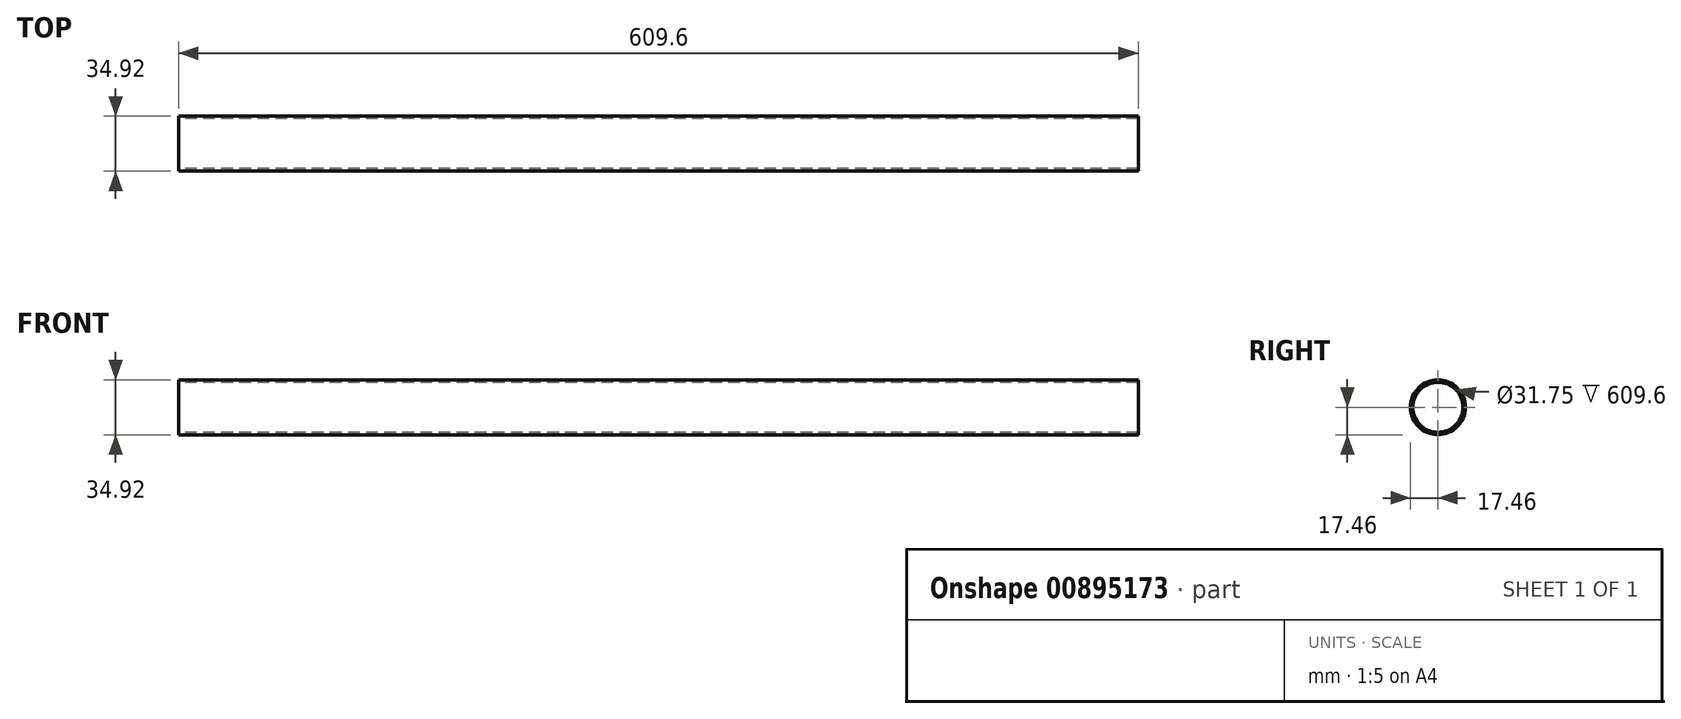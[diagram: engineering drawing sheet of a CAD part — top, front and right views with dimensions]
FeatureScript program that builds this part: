
annotation { "Feature Type Name" : "Feature", "Feature Type Description" : "" }
export const myFeature = defineFeature(function(context is Context, id is Id, definition is map)
    precondition{}
    {
        {
            var Q0;
            Q0=qCreatedBy(makeId("Right.planeOp"),FACE);
            var sketch = newSketch(context, id + "F0", { "sketchPlane" : qUnion([Q0])});
            skCircle(sketch, "E0", {"center": v(0, 0) * mm, "radius": 15.88 * mm});
            skCircle(sketch, "E1", {"center": v(0, 0) * mm, "radius": 17.46 * mm});
            skSolve(sketch);
        }
        {
            var Q0;
            Q0=qSketchRegion(id+"F0",true);
            extrude(context, id + "F1", {"entities" : qUnion([Q0]), "depth" : 609.6 * mm, "offsetDistance" : 25 * mm});
        }
    });
